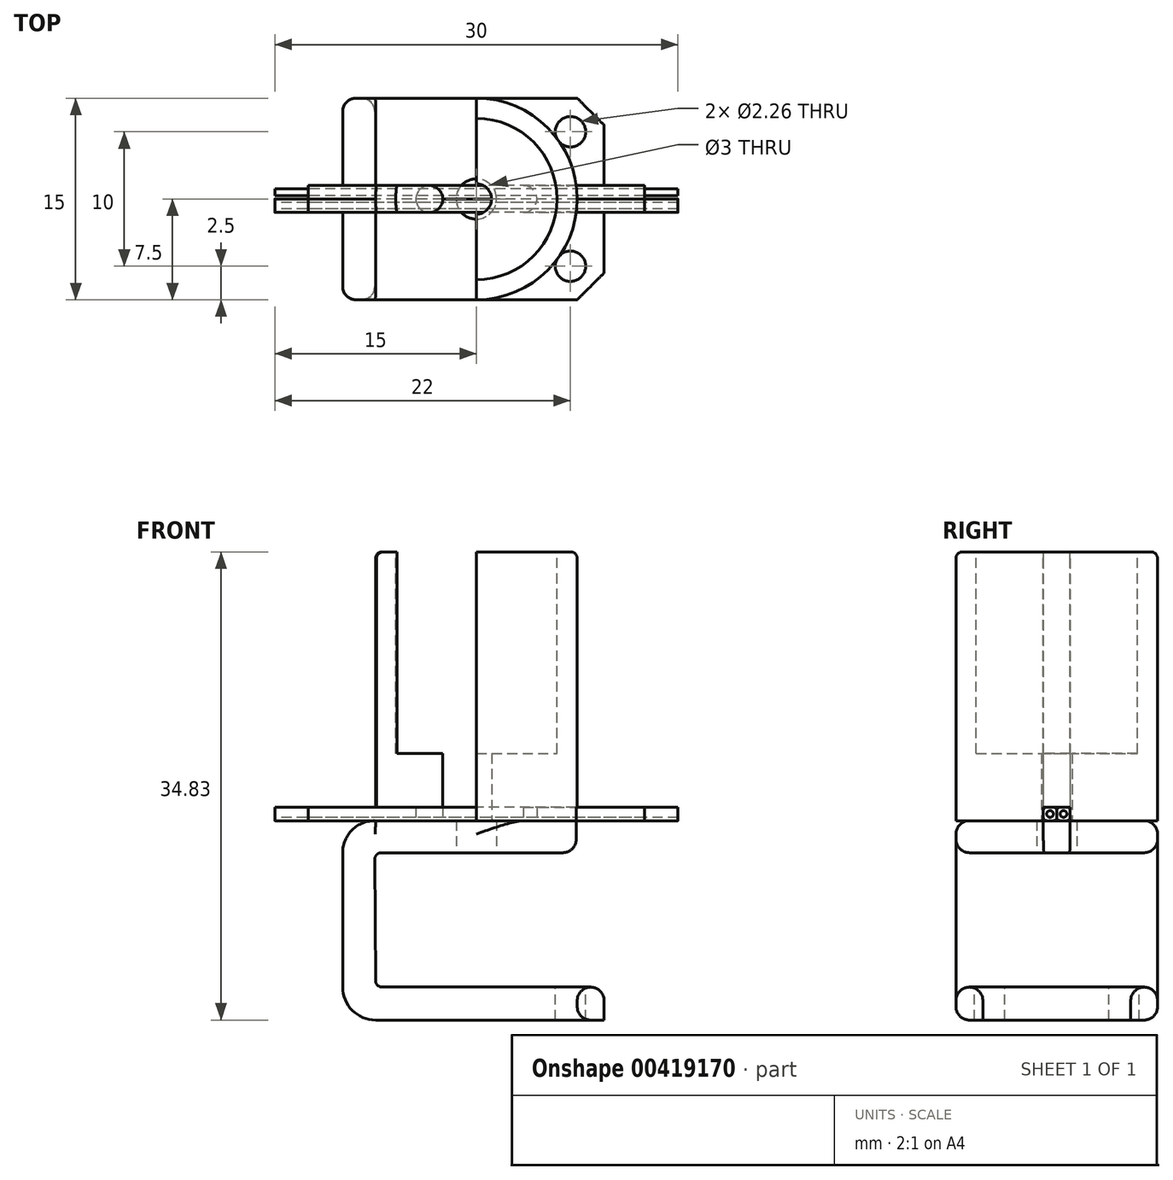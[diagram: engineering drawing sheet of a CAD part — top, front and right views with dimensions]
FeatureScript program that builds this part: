
annotation { "Feature Type Name" : "Feature", "Feature Type Description" : "" }
export const myFeature = defineFeature(function(context is Context, id is Id, definition is map)
    precondition{}
    {
        {
            var Q0;
            Q0=qCreatedBy(makeId("Top.planeOp"),FACE);
            var sketch = newSketch(context, id + "F0", { "sketchPlane" : qUnion([Q0])});
            skCircle(sketch, "E0", {"center": v(0, 0) * mm, "radius": 7.5 * mm});
            skSolve(sketch);
        }
        {
            var Q0;
            Q0=makeQuery(id+"F0.imprint","IMPRINT",FACE,{"disambiguationData":[TD([[makeQuery(id+"F0.imprint","IMPRINT",EDGE,{"derivedFrom":sQuery(id+"F0.wireOp",EDGE,"E0")}),1.0]])]});
            extrude(context, id + "F1", {"entities" : qUnion([Q0]), "depth" : 20 * mm});
        }
        {
            var Q0;
            Q0=makeQuery(id+"F1.opExtrude","CAP_FACE",FACE,{"disambiguationData":[OSD([sQuery(id+"F0.wireOp",EDGE,"E0")])],"isStart":false});
            var sketch = newSketch(context, id + "F2", { "sketchPlane" : qUnion([Q0])});
            skCircle(sketch, "E1", {"center": v(0, 0) * mm, "radius": 6 * mm});
            skSolve(sketch);
        }
        {
            var Q0;
            Q0 = qSketchRegion(id + "F2", true);
            extrude(context, id + "F3", {"entities" : qUnion([Q0]), "operationType" : NewBodyOperationType.REMOVE, "oppositeDirection" : true, "depth" : 15 * mm});
        }
        {
            var Q0;
            Q0=makeQuery(id+"F1.opExtrude","CAP_FACE",FACE,{"disambiguationData":[OSD([sQuery(id+"F0.wireOp",EDGE,"E0")])],"isStart":true});
            var sketch = newSketch(context, id + "F4", { "sketchPlane" : qUnion([Q0])});
            skLineSegment(sketch, "E2", {"start": v(0, -1) * mm, "end": v(0, 1) * mm});
            skLineSegment(sketch, "E3", {"start": v(0, 0) * mm, "end": v(17.94, 0) * mm});
            skLineSegment(sketch, "E4", {"start": v(0, 1) * mm, "end": v(0.53, 1) * mm});
            skLineSegment(sketch, "E5", {"start": v(0, -1) * mm, "end": v(0.53, -1) * mm});
            skLineSegment(sketch, "E6", {"start": v(0, 0) * mm, "end": v(1.13, 0) * mm});
            skCircle(sketch, "E7", {"center": v(3.5, 0) * mm, "radius": 1 * mm});
            skCircle(sketch, "E8", {"center": v(0, 0) * mm, "radius": 1.13 * mm});
            skLineSegment(sketch, "E9.trimOffspring", {"start": v(3.5, -1) * mm, "end": v(7.43, -1) * mm});
            skLineSegment(sketch, "E10.trimOffspring", {"start": v(3.5, 1) * mm, "end": v(7.43, 1) * mm});
            skLineSegment(sketch, "E11.trimOffspring", {"start": v(2.5, 0) * mm, "end": v(3.5, 0) * mm});
            skLineSegment(sketch, "E12.MirrorCS", {"start": v(-2.5, 0) * mm, "end": v(-3.5, 0) * mm});
            skCircle(sketch, "E13.MirrorC", {"center": v(-3.5, 0) * mm, "radius": 1 * mm});
            skLineSegment(sketch, "E14.MirrorCS", {"start": v(-3.5, 1) * mm, "end": v(-7.43, 1) * mm});
            skLineSegment(sketch, "E15.MirrorCS", {"start": v(-3.5, -1) * mm, "end": v(-7.43, -1) * mm});
            skLineSegment(sketch, "E16", {"start": v(0, 0) * mm, "end": v(0, 7.5) * mm});
            skLineSegment(sketch, "E17", {"start": v(0, 0) * mm, "end": v(0, -7.5) * mm});
            skLineSegment(sketch, "E18", {"start": v(0, 7.5) * mm, "end": v(10, 7.5) * mm});
            skLineSegment(sketch, "E19", {"start": v(10, 7.5) * mm, "end": v(10, -7.5) * mm});
            skLineSegment(sketch, "E20", {"start": v(10, -7.5) * mm, "end": v(0, -7.5) * mm});
            skSolve(sketch);
        }
        {
            var Q0;
            {var subQ0=sQuery(id+"F4.wireOp",EDGE,"E13.MirrorC");var subQ1=makeQuery(id+"F4.imprint","IMPRINT",VERTEX,{"derivedFrom":subQ0});Q0=makeQuery(id+"F4.imprint","IMPRINT",FACE,{"disambiguationData":[TD([[makeQuery(id+"F4.imprint","IMPRINT",EDGE,{"disambiguationData":[TD([[subQ1,1.0]])],"derivedFrom":subQ0}),-1.0]])]});}
            var Q1;
            {var subQ0=sQuery(id+"F4.wireOp",EDGE,"E4");Q1=makeQuery(id+"F4.imprint","IMPRINT",FACE,{"disambiguationData":[TD([[makeQuery(id+"F4.imprint","IMPRINT",EDGE,{"derivedFrom":subQ0}),1.0]])]});}
            var Q2;
            {var subQ0=sQuery(id+"F4.wireOp",EDGE,"E5");Q2=makeQuery(id+"F4.imprint","IMPRINT",FACE,{"disambiguationData":[TD([[makeQuery(id+"F4.imprint","IMPRINT",EDGE,{"derivedFrom":subQ0}),-1.0]])]});}
            var Q3;
            {var subQ2=sQuery(id+"F4.wireOp",EDGE,"E16");var subQ5=sQuery(id+"F4.wireOp",EDGE,"E8");var subQ6=makeQuery(id+"F4.imprint","INTERSECT",VERTEX,{"derivedFrom":[subQ5,subQ2]});Q3=makeQuery(id+"F4.imprint","IMPRINT",FACE,{"disambiguationData":[TD([[makeQuery(id+"F4.imprint","IMPRINT",EDGE,{"disambiguationData":[TD([[subQ6,-1.0]])],"derivedFrom":subQ5}),1.0]])]});}
            var Q4;
            {var subQ1=sQuery(id+"F4.wireOp",EDGE,"E18");Q4=makeQuery(id+"F4.imprint","IMPRINT",FACE,{"disambiguationData":[TD([[makeQuery(id+"F4.imprint","IMPRINT",EDGE,{"derivedFrom":subQ1}),-1.0]])]});}
            var Q5;
            {var subQ2=sQuery(id+"F4.wireOp",EDGE,"E20");Q5=makeQuery(id+"F4.imprint","IMPRINT",FACE,{"disambiguationData":[TD([[makeQuery(id+"F4.imprint","IMPRINT",EDGE,{"derivedFrom":subQ2}),-1.0]])]});}
            var Q6;
            {var subQ0=sQuery(id+"F4.wireOp",EDGE,"E11.trimOffspring");Q6=makeQuery(id+"F4.imprint","IMPRINT",FACE,{"disambiguationData":[TD([[makeQuery(id+"F4.imprint","IMPRINT",EDGE,{"derivedFrom":subQ0}),1.0]])]});}
            var Q7;
            {var subQ0=sQuery(id+"F4.wireOp",EDGE,"E11.trimOffspring");Q7=makeQuery(id+"F4.imprint","IMPRINT",FACE,{"disambiguationData":[TD([[makeQuery(id+"F4.imprint","IMPRINT",EDGE,{"derivedFrom":subQ0}),-1.0]])]});}
            var Q8;
            {var subQ0=sQuery(id+"F4.wireOp",EDGE,"E5");Q8=makeQuery(id+"F4.imprint","IMPRINT",FACE,{"disambiguationData":[TD([[makeQuery(id+"F4.imprint","IMPRINT",EDGE,{"derivedFrom":subQ0}),1.0]])]});}
            var Q9;
            {var subQ0=sQuery(id+"F4.wireOp",EDGE,"E4");Q9=makeQuery(id+"F4.imprint","IMPRINT",FACE,{"disambiguationData":[TD([[makeQuery(id+"F4.imprint","IMPRINT",EDGE,{"derivedFrom":subQ0}),-1.0]])]});}
            extrude(context, id + "F5", {"entities" : qUnion([Q0, Q1, Q2, Q3, Q4, Q5, Q6, Q7, Q8, Q9]), "operationType" : NewBodyOperationType.REMOVE, "oppositeDirection" : true, "depth" : 25 * mm});
        }
        {
            var Q0;
            {var subQ0=sQuery(id+"F4.wireOp",EDGE,"E14.MirrorCS");Q0=makeQuery(id+"F4.imprint","IMPRINT",FACE,{"disambiguationData":[TD([[makeQuery(id+"F4.imprint","IMPRINT",EDGE,{"derivedFrom":subQ0}),1.0]])]});}
            var Q1;
            {var subQ5=sQuery(id+"F4.wireOp",EDGE,"E10.trimOffspring");Q1=makeQuery(id+"F4.imprint","IMPRINT",FACE,{"disambiguationData":[TD([[makeQuery(id+"F4.imprint","IMPRINT",EDGE,{"derivedFrom":subQ5}),-1.0]])]});}
            var Q2;
            {var subQ5=sQuery(id+"F4.wireOp",EDGE,"E9.trimOffspring");Q2=makeQuery(id+"F4.imprint","IMPRINT",FACE,{"disambiguationData":[TD([[makeQuery(id+"F4.imprint","IMPRINT",EDGE,{"derivedFrom":subQ5}),1.0]])]});}
            extrude(context, id + "F6", {"entities" : qUnion([Q0, Q1, Q2]), "operationType" : NewBodyOperationType.REMOVE, "oppositeDirection" : true, "depth" : 1 * mm});
        }
        {
            var Q0;
            Q0=makeQuery(id+"F3.boolean.opBoolean","COPY",EDGE,{"derivedFrom":makeQuery(id+"F3.opExtrude","CAP_EDGE",EDGE,{"disambiguationData":[OSD([sQuery(id+"F2.wireOp",EDGE,"E1")])],"isStart":true})});
            var Q1;
            Q1=makeQuery(id+"F1.opExtrude","CAP_EDGE",EDGE,{"disambiguationData":[OSD([sQuery(id+"F0.wireOp",EDGE,"E0")])],"isStart":false});
            fillet(context, id + "F7", {"entities" : qUnion([Q0, Q1]), "radius" : .5 * mm, "tangentPropagation" : true, "allowEdgeOverflow" : false});
        }
        {
            var Q0;
            {var subQ5=sQuery(id+"F4.wireOp",EDGE,"E9.trimOffspring");Q0=makeQuery(id+"F4.imprint","IMPRINT",FACE,{"disambiguationData":[TD([[makeQuery(id+"F4.imprint","IMPRINT",EDGE,{"derivedFrom":subQ5}),-1.0]])]});}
            var sketch = newSketch(context, id + "F8", { "sketchPlane" : qUnion([Q0])});
            skCircle(sketch, "E21", {"center": v(0, 0) * mm, "radius": 7.5 * mm});
            skLineSegment(sketch, "E22", {"start": v(0, 0) * mm, "end": v(0, 7.5) * mm});
            skLineSegment(sketch, "E23", {"start": v(0, 7.5) * mm, "end": v(-7.5, 7.5) * mm});
            skLineSegment(sketch, "E24", {"start": v(0, 0) * mm, "end": v(0, -7.5) * mm});
            skLineSegment(sketch, "E25", {"start": v(0, -7.5) * mm, "end": v(-7.5, -7.5) * mm});
            skSolve(sketch);
        }
        {
            var Q0;
            Q0=sQuery(id+"F8.wireOp",EDGE,"E23");
            cPlane(context, id + "F9", {"entities" : qUnion([Q0]), "cplaneType" : CPlaneType.LINE_ANGLE, "offset" : 25 * mm, "angle" : 0 * degree, "width" : 150 * mm, "height" : 150 * mm});
        }
        {
            var Q0;
            Q0=qCreatedBy(id+"F9.planeOp",FACE);
            var sketch = newSketch(context, id + "F10", { "sketchPlane" : qUnion([Q0])});
            skLineSegment(sketch, "E26", {"start": v(7.43, 0) * mm, "end": v(7.43, -2.38) * mm});
            skLineSegment(sketch, "E27", {"start": v(7.43, 0) * mm, "end": v(-7.5, 0) * mm});
            skLineSegment(sketch, "E28", {"start": v(7.43, -2.38) * mm, "end": v(-7.06, -2.38) * mm});
            skArc(sketch, "E29", {"start": v(-7.5, 0) * mm, "mid": v(-9.23, -0.67) * mm, "end": v(-9.95, -2.38) * mm});
            skLineSegment(sketch, "E30", {"start": v(-9.95, -2.38) * mm, "end": v(-9.95, -12.38) * mm});
            skLineSegment(sketch, "E31", {"start": v(-7.56, -2.88) * mm, "end": v(-7.5, -11.88) * mm});
            skArc(sketch, "E32", {"start": v(-9.95, -12.38) * mm, "mid": v(-9.23, -14.11) * mm, "end": v(-7.5, -14.83) * mm});
            skLineSegment(sketch, "E33", {"start": v(-7.5, -14.83) * mm, "end": v(9.5, -14.83) * mm});
            skLineSegment(sketch, "E34", {"start": v(9.5, -14.83) * mm, "end": v(9.5, -12.38) * mm});
            skLineSegment(sketch, "E35", {"start": v(9.5, -12.38) * mm, "end": v(-7, -12.38) * mm});
            skArc(sketch, "E36.filletArc", {"start": v(-7.06, -2.38) * mm, "mid": v(-7.42, -2.53) * mm, "end": v(-7.56, -2.88) * mm});
            skArc(sketch, "E37.filletArc", {"start": v(-7.5, -11.88) * mm, "mid": v(-7.36, -12.24) * mm, "end": v(-7, -12.38) * mm});
            skSolve(sketch);
        }
        {
            var Q0;
            Q0 = qSketchRegion(id + "F10", true);
            extrude(context, id + "F11", {"entities" : qUnion([Q0]), "oppositeDirection" : true, "depth" : 15 * mm});
        }
        {
            var Q0;
            {var subQ1=sQuery(id+"F4.wireOp",EDGE,"E18");Q0=makeQuery(id+"F4.imprint","IMPRINT",FACE,{"disambiguationData":[TD([[makeQuery(id+"F4.imprint","IMPRINT",EDGE,{"derivedFrom":subQ1}),-1.0]])]});}
            var Q1;
            {var subQ2=sQuery(id+"F4.wireOp",EDGE,"E20");Q1=makeQuery(id+"F4.imprint","IMPRINT",FACE,{"disambiguationData":[TD([[makeQuery(id+"F4.imprint","IMPRINT",EDGE,{"derivedFrom":subQ2}),-1.0]])]});}
            extrude(context, id + "F12", {"entities" : qUnion([Q0, Q1]), "operationType" : NewBodyOperationType.REMOVE, "depth" : 5 * mm});
        }
        {
            var Q0;
            Q0=makeQuery(id+"F11.opExtrude","SWEPT_FACE",FACE,{"disambiguationData":[OSD([sQuery(id+"F10.wireOp",EDGE,"E28")])]});
            var sketch = newSketch(context, id + "F13", { "sketchPlane" : qUnion([Q0])});
            skCircle(sketch, "E38", {"center": v(0, 0) * mm, "radius": 1.5 * mm});
            skSolve(sketch);
        }
        {
            var Q0;
            Q0=makeQuery(id+"F13.imprint","IMPRINT",FACE,{"disambiguationData":[TD([[makeQuery(id+"F13.imprint","IMPRINT",EDGE,{"derivedFrom":sQuery(id+"F13.wireOp",EDGE,"E38")}),1.0]])]});
            extrude(context, id + "F14", {"entities" : qUnion([Q0]), "operationType" : NewBodyOperationType.REMOVE, "oppositeDirection" : true, "depth" : 2.38 * mm});
        }
        {
            var Q0;
            Q0=makeQuery(id+"F11.opExtrude","SWEPT_FACE",FACE,{"disambiguationData":[OSD([sQuery(id+"F10.wireOp",EDGE,"E35")])]});
            var sketch = newSketch(context, id + "F15", { "sketchPlane" : qUnion([Q0])});
            skLineSegment(sketch, "E39", {"start": v(9.5, -7.5) * mm, "end": v(9.5, -5) * mm});
            skLineSegment(sketch, "E40", {"start": v(9.5, -5) * mm, "end": v(7, -5) * mm});
            skCircle(sketch, "E41", {"center": v(7, -5) * mm, "radius": 1.13 * mm});
            skLineSegment(sketch, "E42", {"start": v(9.5, 0) * mm, "end": v(2.48, 0) * mm});
            skPoint(sketch, "E42.endSnap0", {"position": v(9.5, 0) * mm});
            skCircle(sketch, "E43.MirrorC", {"center": v(7, 5) * mm, "radius": 1.13 * mm});
            skSolve(sketch);
        }
        {
            var Q0;
            Q0 = qSketchRegion(id + "F15", true);
            extrude(context, id + "F16", {"entities" : qUnion([Q0]), "operationType" : NewBodyOperationType.REMOVE, "oppositeDirection" : true, "depth" : 25 * mm});
        }
        {
            var Q0;
            Q0=makeQuery(id+"F11.opExtrude","CAP_EDGE",EDGE,{"disambiguationData":[OSD([sQuery(id+"F10.wireOp",EDGE,"E34")])],"isStart":true});
            var Q1;
            Q1=makeQuery(id+"F11.opExtrude","CAP_EDGE",EDGE,{"disambiguationData":[OSD([sQuery(id+"F10.wireOp",EDGE,"E34")])],"isStart":false});
            chamfer(context, id + "F17", {"entities" : qUnion([Q0, Q1]), "width" : 2 * mm, "tangentPropagation" : true});
        }
        {
            var Q0;
            Q0=makeQuery(id+"F11.opExtrude","CAP_EDGE",EDGE,{"disambiguationData":[OSD([sQuery(id+"F10.wireOp",EDGE,"E30")])],"isStart":true});
            var Q1;
            Q1=makeQuery(id+"F11.opExtrude","CAP_EDGE",EDGE,{"disambiguationData":[OSD([sQuery(id+"F10.wireOp",EDGE,"E29")])],"isStart":true});
            var Q2;
            Q2=makeQuery(id+"F11.opExtrude","CAP_EDGE",EDGE,{"disambiguationData":[OSD([sQuery(id+"F10.wireOp",EDGE,"E29")])],"isStart":false});
            fillet(context, id + "F18", {"entities" : qUnion([Q0, Q1, Q2]), "radius" : 1 * mm, "tangentPropagation" : true, "allowEdgeOverflow" : false});
        }
        {
            var Q0;
            Q0=makeQuery(id+"F11.opExtrude","SWEPT_EDGE",EDGE,{"disambiguationData":[OSD([sQuery(id+"F10.wireOp",EDGE,"E34"),sQuery(id+"F10.wireOp",EDGE,"E35")])]});
            var Q1;
            Q1=makeQuery(id+"F11.opExtrude","SWEPT_EDGE",EDGE,{"disambiguationData":[OSD([sQuery(id+"F10.wireOp",EDGE,"E26"),sQuery(id+"F10.wireOp",EDGE,"E28")])]});
            var Q2;
            Q2=makeQuery(id+"F12.boolean.opBoolean","INTERSECT",EDGE,{"disambiguationData":[OD(0.0)],"derivedFrom":[makeQuery(id+"F11.opExtrude","SWEPT_FACE",FACE,{"disambiguationData":[OSD([sQuery(id+"F10.wireOp",EDGE,"E28")])]}),makeQuery(id+"F12.opExtrude","SWEPT_FACE",FACE,{"disambiguationData":[OSD([sQuery(id+"F0.wireOp",EDGE,"E0")])]})]});
            var Q3;
            Q3=makeQuery(id+"F12.boolean.opBoolean","INTERSECT",EDGE,{"disambiguationData":[OD(1.0)],"derivedFrom":[makeQuery(id+"F11.opExtrude","SWEPT_FACE",FACE,{"disambiguationData":[OSD([sQuery(id+"F10.wireOp",EDGE,"E28")])]}),makeQuery(id+"F12.opExtrude","SWEPT_FACE",FACE,{"disambiguationData":[OSD([sQuery(id+"F0.wireOp",EDGE,"E0")])]})]});
            fillet(context, id + "F19", {"entities" : qUnion([Q0, Q1, Q2, Q3]), "radius" : 1 * mm, "tangentPropagation" : true, "allowEdgeOverflow" : false});
        }
        {
            var Q0;
            Q0=qCreatedBy(makeId("Right.planeOp"),FACE);
            var sketch = newSketch(context, id + "F20", { "sketchPlane" : qUnion([Q0])});
            skLineSegment(sketch, "E44.bottom", {"start": v(-0.75, 0) * mm, "end": v(-0.25, 0) * mm});
            skLineSegment(sketch, "E44.top", {"start": v(-0.75, 1) * mm, "end": v(-0.25, 1) * mm});
            skLineSegment(sketch, "E44.left", {"start": v(-1, 0.25) * mm, "end": v(-1, 0.75) * mm});
            skLineSegment(sketch, "E44.right", {"start": v(1, 0.25) * mm, "end": v(1, 0.75) * mm});
            skLineSegment(sketch, "E45", {"start": v(0, 0.25) * mm, "end": v(0, 0.75) * mm});
            skLineSegment(sketch, "E46", {"start": v(0, 0.75) * mm, "end": v(0, 0.5) * mm});
            skLineSegment(sketch, "E47", {"start": v(0.5, 0.5) * mm, "end": v(0, 0.5) * mm});
            skCircle(sketch, "E48", {"center": v(0.5, 0.5) * mm, "radius": 0.25 * mm});
            skCircle(sketch, "E49.MirrorC", {"center": v(-0.5, 0.5) * mm, "radius": 0.25 * mm});
            skPoint(sketch, "E50.visualSharp", {"position": v(-1, 1) * mm});
            skArc(sketch, "E50.filletArc", {"start": v(-0.75, 1) * mm, "mid": v(-0.93, 0.93) * mm, "end": v(-1, 0.75) * mm});
            skPoint(sketch, "E51.visualSharp", {"position": v(1, 1) * mm});
            skArc(sketch, "E51.filletArc", {"start": v(1, 0.75) * mm, "mid": v(0.93, 0.93) * mm, "end": v(0.75, 1) * mm});
            skPoint(sketch, "E52.visualSharp", {"position": v(1, 0) * mm});
            skArc(sketch, "E52.filletArc", {"start": v(0.75, 0) * mm, "mid": v(0.93, 0.07) * mm, "end": v(1, 0.25) * mm});
            skPoint(sketch, "E53.visualSharp", {"position": v(-1, 0) * mm});
            skArc(sketch, "E53.filletArc", {"start": v(-1, 0.25) * mm, "mid": v(-0.93, 0.07) * mm, "end": v(-0.75, 0) * mm});
            skArc(sketch, "E54.filletArc", {"start": v(0, 0.75) * mm, "mid": v(-0.07, 0.93) * mm, "end": v(-0.25, 1) * mm});
            skPoint(sketch, "E55.newPointA", {"position": v(0, 0) * mm});
            skArc(sketch, "E55.filletArc", {"start": v(-0.25, 0) * mm, "mid": v(-0.07, 0.07) * mm, "end": v(0, 0.25) * mm});
            skLineSegment(sketch, "E56", {"start": v(0, 0.25) * mm, "end": v(0, 1) * mm});
            skLineSegment(sketch, "E57", {"start": v(0.75, 1) * mm, "end": v(0.25, 1) * mm});
            skLineSegment(sketch, "E58", {"start": v(0.75, 0) * mm, "end": v(0.25, 0) * mm});
            skPoint(sketch, "E59.visualSharp", {"position": v(0, 1) * mm});
            skArc(sketch, "E59.filletArc", {"start": v(0.25, 1) * mm, "mid": v(0.07, 0.93) * mm, "end": v(0, 0.75) * mm});
            skArc(sketch, "E60.filletArc", {"start": v(0, 0.25) * mm, "mid": v(0.07, 0.07) * mm, "end": v(0.25, 0) * mm});
            skSolve(sketch);
        }
        {
            var Q0;
            Q0 = qSketchRegion(id + "F20", true);
            var Q1;
            Q1=makeQuery(id+"F20.imprint","IMPRINT",FACE,{"disambiguationData":[TD([[makeQuery(id+"F20.imprint","IMPRINT",EDGE,{"derivedFrom":sQuery(id+"F20.wireOp",EDGE,"E49.MirrorC")}),-1.0]])]});
            var Q2;
            Q2=makeQuery(id+"F20.imprint","IMPRINT",FACE,{"disambiguationData":[TD([[makeQuery(id+"F20.imprint","IMPRINT",EDGE,{"derivedFrom":sQuery(id+"F20.wireOp",EDGE,"E48")}),1.0]])]});
            extrude(context, id + "F21", {"entities" : qUnion([Q0, Q1, Q2]), "endBound" : BoundingType.SYMMETRIC, "depth" : 25 * mm});
        }
        {
            var Q0;
            Q0=makeQuery(id+"F20.imprint","IMPRINT",FACE,{"disambiguationData":[TD([[makeQuery(id+"F20.imprint","IMPRINT",EDGE,{"derivedFrom":sQuery(id+"F20.wireOp",EDGE,"E49.MirrorC")}),-1.0]])]});
            var Q1;
            Q1=makeQuery(id+"F20.imprint","IMPRINT",FACE,{"disambiguationData":[TD([[makeQuery(id+"F20.imprint","IMPRINT",EDGE,{"derivedFrom":sQuery(id+"F20.wireOp",EDGE,"E48")}),1.0]])]});
            extrude(context, id + "F22", {"entities" : qUnion([Q0, Q1]), "endBound" : BoundingType.SYMMETRIC, "depth" : 30 * mm});
        }
    });
